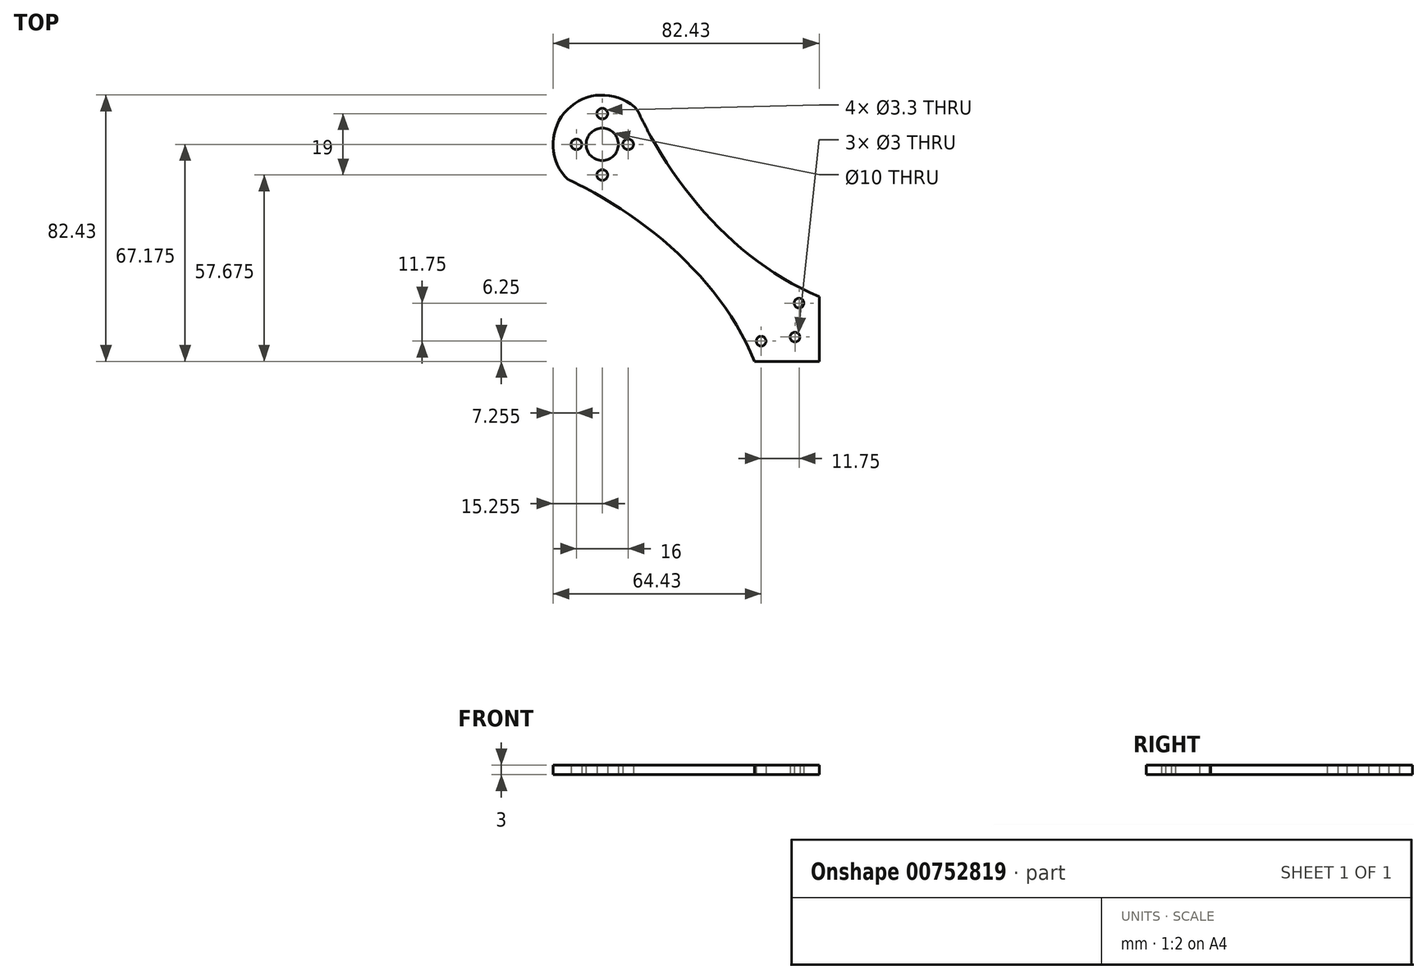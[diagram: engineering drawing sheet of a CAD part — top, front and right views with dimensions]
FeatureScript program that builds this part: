
annotation { "Feature Type Name" : "Feature", "Feature Type Description" : "" }
export const myFeature = defineFeature(function(context is Context, id is Id, definition is map)
    precondition{}
    {
        {
            var Q0;
            Q0=qCreatedBy(makeId("Top.planeOp"),FACE);
            var sketch = newSketch(context, id + "F0", { "sketchPlane" : qUnion([Q0])});
            skLineSegment(sketch, "E0.bottom", {"start": v(18, 18) * mm, "end": v(-18, 18) * mm, "construction": true});
            skLineSegment(sketch, "E0.top", {"start": v(18, -18) * mm, "end": v(-18, -18) * mm, "construction": true});
            skLineSegment(sketch, "E0.left", {"start": v(18, 18) * mm, "end": v(18, -18) * mm, "construction": true});
            skLineSegment(sketch, "E0.right", {"start": v(-18, 18) * mm, "end": v(-18, -18) * mm, "construction": true});
            skPoint(sketch, "E0.middle", {"position": v(0, 0) * mm});
            skLineSegment(sketch, "E1.bottom", {"start": v(15.25, 15.25) * mm, "end": v(-15.25, 15.25) * mm, "construction": true});
            skLineSegment(sketch, "E1.top", {"start": v(15.25, -15.25) * mm, "end": v(-15.25, -15.25) * mm, "construction": true});
            skLineSegment(sketch, "E1.left", {"start": v(15.25, 15.25) * mm, "end": v(15.25, -15.25) * mm, "construction": true});
            skLineSegment(sketch, "E1.right", {"start": v(-15.25, 15.25) * mm, "end": v(-15.25, -15.25) * mm, "construction": true});
            skCircle(sketch, "E2", {"center": v(-15.25, 15.25) * mm, "radius": 1.5 * mm, "construction": true});
            skCircle(sketch, "E3", {"center": v(15.25, 15.25) * mm, "radius": 1.5 * mm, "construction": true});
            skCircle(sketch, "E4", {"center": v(15.25, -15.25) * mm, "radius": 1.5 * mm, "construction": true});
            skCircle(sketch, "E5", {"center": v(-15.25, -15.25) * mm, "radius": 1.5 * mm, "construction": true});
            skLineSegment(sketch, "E6", {"start": v(0, 0) * mm, "end": v(-67.18, 67.18) * mm, "construction": true});
            skLineSegment(sketch, "E7", {"start": v(0, 0) * mm, "end": v(67.18, 67.18) * mm, "construction": true});
            skLineSegment(sketch, "E8", {"start": v(0, 0) * mm, "end": v(-67.18, -67.18) * mm, "construction": true});
            skLineSegment(sketch, "E9", {"start": v(0, 0) * mm, "end": v(67.18, -67.18) * mm, "construction": true});
            skCircle(sketch, "E10", {"center": v(-67.18, 67.18) * mm, "radius": 5 * mm});
            skCircle(sketch, "E11", {"center": v(-75.18, 67.18) * mm, "radius": 1.65 * mm});
            skCircle(sketch, "E12", {"center": v(-67.18, 76.68) * mm, "radius": 1.65 * mm});
            skCircle(sketch, "E13", {"center": v(-59.18, 67.18) * mm, "radius": 1.65 * mm});
            skCircle(sketch, "E14", {"center": v(-67.18, 57.68) * mm, "radius": 1.65 * mm});
            skCircle(sketch, "E15", {"center": v(67.18, 67.18) * mm, "radius": 5 * mm});
            skCircle(sketch, "E16", {"center": v(59.18, 67.18) * mm, "radius": 1.65 * mm});
            skCircle(sketch, "E17", {"center": v(67.18, 76.68) * mm, "radius": 1.65 * mm});
            skCircle(sketch, "E18", {"center": v(75.18, 67.18) * mm, "radius": 1.65 * mm});
            skCircle(sketch, "E19", {"center": v(67.18, 57.68) * mm, "radius": 1.65 * mm});
            skCircle(sketch, "E20", {"center": v(67.18, -67.18) * mm, "radius": 5 * mm});
            skCircle(sketch, "E21", {"center": v(59.18, -67.18) * mm, "radius": 1.65 * mm});
            skCircle(sketch, "E22", {"center": v(67.18, -57.68) * mm, "radius": 1.65 * mm});
            skCircle(sketch, "E23", {"center": v(75.18, -67.18) * mm, "radius": 1.65 * mm});
            skCircle(sketch, "E24", {"center": v(67.18, -76.68) * mm, "radius": 1.65 * mm});
            skCircle(sketch, "E25", {"center": v(-67.18, -67.18) * mm, "radius": 5 * mm});
            skCircle(sketch, "E26", {"center": v(-75.18, -67.18) * mm, "radius": 1.65 * mm});
            skCircle(sketch, "E27", {"center": v(-67.18, -57.68) * mm, "radius": 1.65 * mm});
            skCircle(sketch, "E28", {"center": v(-59.18, -67.18) * mm, "radius": 1.65 * mm});
            skCircle(sketch, "E29", {"center": v(-67.18, -76.68) * mm, "radius": 1.65 * mm});
            skCircle(sketch, "E30", {"center": v(-67.18, 67.18) * mm, "radius": 13.3 * mm, "construction": true});
            skCircle(sketch, "E31", {"center": v(-67.18, 67.18) * mm, "radius": 15.25 * mm});
            skCircle(sketch, "E32", {"center": v(67.18, 67.18) * mm, "radius": 13.3 * mm, "construction": true});
            skCircle(sketch, "E33", {"center": v(67.18, 67.18) * mm, "radius": 15.25 * mm});
            skCircle(sketch, "E34", {"center": v(-67.18, -67.18) * mm, "radius": 13.3 * mm, "construction": true});
            skCircle(sketch, "E35", {"center": v(-67.18, -67.18) * mm, "radius": 15.25 * mm});
            skCircle(sketch, "E36", {"center": v(67.18, -67.18) * mm, "radius": 13.3 * mm, "construction": true});
            skCircle(sketch, "E37", {"center": v(67.18, -67.18) * mm, "radius": 15.25 * mm});
            skLineSegment(sketch, "E38.bottom", {"start": v(20, 20) * mm, "end": v(-20, 20) * mm, "construction": true});
            skLineSegment(sketch, "E38.top", {"start": v(20, -20) * mm, "end": v(-20, -20) * mm, "construction": true});
            skLineSegment(sketch, "E38.left", {"start": v(20, 20) * mm, "end": v(20, -20) * mm, "construction": true});
            skLineSegment(sketch, "E38.right", {"start": v(-20, 20) * mm, "end": v(-20, -20) * mm, "construction": true});
            skLineSegment(sketch, "E39", {"start": v(-67.18, 67.18) * mm, "end": v(-77.96, 56.4) * mm, "construction": true});
            skLineSegment(sketch, "E40", {"start": v(-67.18, 67.18) * mm, "end": v(-56.4, 77.96) * mm, "construction": true});
            skPoint(sketch, "E41", {"position": v(0, 20) * mm});
            skPoint(sketch, "E42", {"position": v(-20, 0) * mm});
            skFitSpline(sketch, "E43", {"points": [v(-77.96, 56.4) * mm, v(-20, 0) * mm], "startDerivative": vector(73.8, -34.55) * mm, "endDerivative": vector(31.31, -75.4) * mm});
            skFitSpline(sketch, "E44", {"points": [v(-56.4, 77.96) * mm, v(0, 20) * mm], "startDerivative": vector(34.55, -73.8) * mm, "endDerivative": vector(75.4, -31.31) * mm});
            skLineSegment(sketch, "E45", {"start": v(67.18, 67.18) * mm, "end": v(56.4, 77.96) * mm, "construction": true});
            skLineSegment(sketch, "E46", {"start": v(67.18, 67.18) * mm, "end": v(77.96, 56.4) * mm, "construction": true});
            skFitSpline(sketch, "E47", {"points": [v(56.4, 77.96) * mm, v(0, 20) * mm], "startDerivative": vector(-34.5, -73.75) * mm, "endDerivative": vector(-75.31, -31.22) * mm});
            skFitSpline(sketch, "E48", {"points": [v(77.96, 56.4) * mm, v(20, 0) * mm], "startDerivative": vector(-73.75, -34.5) * mm, "endDerivative": vector(-31.22, -75.31) * mm});
            skCircle(sketch, "E49", {"center": v(-67.18, 67.18) * mm, "radius": 63.5 * mm, "construction": true});
            skCircle(sketch, "E50", {"center": v(67.18, 67.18) * mm, "radius": 63.5 * mm, "construction": true});
            skCircle(sketch, "E51", {"center": v(-67.18, -67.18) * mm, "radius": 63.5 * mm, "construction": true});
            skCircle(sketch, "E52", {"center": v(67.18, -67.18) * mm, "radius": 63.5 * mm, "construction": true});
            skLineSegment(sketch, "E53", {"start": v(67.18, -67.18) * mm, "end": v(56.4, -77.96) * mm, "construction": true});
            skLineSegment(sketch, "E54", {"start": v(67.18, -67.18) * mm, "end": v(77.96, -56.4) * mm, "construction": true});
            skLineSegment(sketch, "E55", {"start": v(-67.18, -67.18) * mm, "end": v(-77.96, -56.4) * mm, "construction": true});
            skLineSegment(sketch, "E56", {"start": v(-67.18, -67.18) * mm, "end": v(-56.4, -77.96) * mm, "construction": true});
            skFitSpline(sketch, "E57", {"points": [v(-77.96, -56.4) * mm, v(-20, 0) * mm], "startDerivative": vector(73.75, 34.5) * mm, "endDerivative": vector(31.22, 75.31) * mm});
            skFitSpline(sketch, "E58", {"points": [v(0, -20) * mm, v(-56.4, -77.96) * mm], "startDerivative": vector(-75.31, -31.22) * mm, "endDerivative": vector(-34.5, -73.75) * mm});
            skFitSpline(sketch, "E59", {"points": [v(0, -20) * mm, v(56.4, -77.96) * mm], "startDerivative": vector(75.31, -31.22) * mm, "endDerivative": vector(34.5, -73.75) * mm});
            skFitSpline(sketch, "E60", {"points": [v(20, 0) * mm, v(77.96, -56.4) * mm], "startDerivative": vector(31.22, -75.31) * mm, "endDerivative": vector(73.75, -34.5) * mm});
            skLineSegment(sketch, "E61", {"start": v(-20, 0) * mm, "end": v(20, 0) * mm});
            skLineSegment(sketch, "E62", {"start": v(0, 20) * mm, "end": v(0, -20) * mm});
            skLineSegment(sketch, "E63.bottom", {"start": v(-7.5, 7.5) * mm, "end": v(7.5, 7.5) * mm, "construction": true});
            skLineSegment(sketch, "E63.top", {"start": v(-7.5, -7.5) * mm, "end": v(7.5, -7.5) * mm, "construction": true});
            skLineSegment(sketch, "E63.left", {"start": v(-7.5, 7.5) * mm, "end": v(-7.5, -7.5) * mm, "construction": true});
            skLineSegment(sketch, "E63.right", {"start": v(7.5, 7.5) * mm, "end": v(7.5, -7.5) * mm, "construction": true});
            skCircle(sketch, "E64", {"center": v(-7.5, 7.5) * mm, "radius": 1.5 * mm});
            skCircle(sketch, "E65", {"center": v(7.5, 7.5) * mm, "radius": 1.5 * mm});
            skCircle(sketch, "E66", {"center": v(7.5, -7.5) * mm, "radius": 1.5 * mm});
            skCircle(sketch, "E67", {"center": v(-7.5, -7.5) * mm, "radius": 1.5 * mm});
            skLineSegment(sketch, "E68.bottom", {"start": v(6.25, 18) * mm, "end": v(-6.25, 18) * mm, "construction": true});
            skLineSegment(sketch, "E68.top", {"start": v(6.25, -18) * mm, "end": v(-6.25, -18) * mm, "construction": true});
            skLineSegment(sketch, "E68.left", {"start": v(6.25, 18) * mm, "end": v(6.25, -18) * mm, "construction": true});
            skLineSegment(sketch, "E68.right", {"start": v(-6.25, 18) * mm, "end": v(-6.25, -18) * mm, "construction": true});
            skCircle(sketch, "E69", {"center": v(-6.25, 18) * mm, "radius": 1.5 * mm});
            skCircle(sketch, "E70", {"center": v(6.25, 18) * mm, "radius": 1.5 * mm});
            skCircle(sketch, "E71", {"center": v(-6.25, -18) * mm, "radius": 1.5 * mm});
            skCircle(sketch, "E72", {"center": v(6.25, -18) * mm, "radius": 1.5 * mm});
            skLineSegment(sketch, "E73.bottom", {"start": v(-18, 6.25) * mm, "end": v(18, 6.25) * mm, "construction": true});
            skLineSegment(sketch, "E73.top", {"start": v(-18, -6.25) * mm, "end": v(18, -6.25) * mm, "construction": true});
            skLineSegment(sketch, "E73.left", {"start": v(-18, 6.25) * mm, "end": v(-18, -6.25) * mm, "construction": true});
            skLineSegment(sketch, "E73.right", {"start": v(18, 6.25) * mm, "end": v(18, -6.25) * mm, "construction": true});
            skCircle(sketch, "E74", {"center": v(-18, 6.25) * mm, "radius": 1.5 * mm});
            skCircle(sketch, "E75", {"center": v(-18, -6.25) * mm, "radius": 1.5 * mm});
            skCircle(sketch, "E76", {"center": v(18, 6.25) * mm, "radius": 1.5 * mm});
            skCircle(sketch, "E77", {"center": v(18, -6.25) * mm, "radius": 1.5 * mm});
            skSolve(sketch);
        }
        {
            var Q0;
            Q0=makeQuery(id+"F0.imprint","IMPRINT",FACE,{"disambiguationData":[TD([[makeQuery(id+"F0.imprint","IMPRINT",EDGE,{"derivedFrom":sQuery(id+"F0.wireOp",EDGE,"E64")}),-1.0]])]});
            var Q1;
            Q1=makeQuery(id+"F0.imprint","IMPRINT",FACE,{"disambiguationData":[TD([[makeQuery(id+"F0.imprint","IMPRINT",EDGE,{"derivedFrom":sQuery(id+"F0.wireOp",EDGE,"E10")}),-1.0]])]});
            extrude(context, id + "F1", {"entities" : qUnion([Q0, Q1]), "depth" : 3 * mm, "offsetDistance" : 25 * mm});
        }
        {
            var Q0;
            Q0=makeQuery(id+"F1.opExtrude","SWEPT_EDGE",EDGE,{"disambiguationData":[OSD([sQuery(id+"F0.wireOp",EDGE,"E31"),sQuery(id+"F0.wireOp",EDGE,"E44")])]});
            var Q1;
            Q1=makeQuery(id+"F1.opExtrude","SWEPT_EDGE",EDGE,{"disambiguationData":[OSD([sQuery(id+"F0.wireOp",EDGE,"E31"),sQuery(id+"F0.wireOp",EDGE,"E43")])]});
            fillet(context, id + "F2", {"entities" : qUnion([Q0, Q1]), "radius" : 5 * mm, "tangentPropagation" : true, "allowEdgeOverflow" : false});
        }
    });
